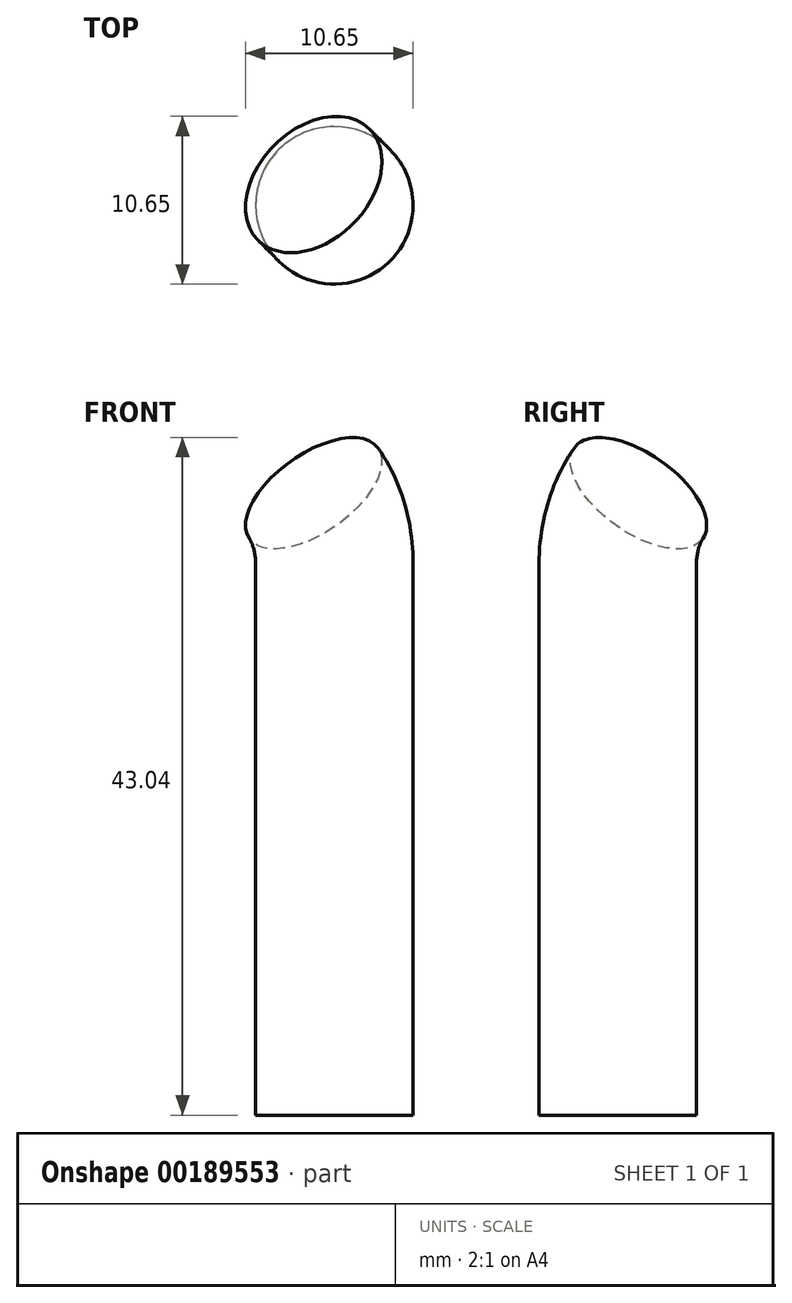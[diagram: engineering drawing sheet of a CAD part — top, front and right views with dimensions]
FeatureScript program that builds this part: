
annotation { "Feature Type Name" : "Feature", "Feature Type Description" : "" }
export const myFeature = defineFeature(function(context is Context, id is Id, definition is map)
    precondition{}
    {
        {
            var Q0;
            Q0=qCreatedBy(makeId("Top.planeOp"),FACE);
            var sketch = newSketch(context, id + "F0", { "sketchPlane" : qUnion([Q0])});
            skCircle(sketch, "E0", {"center": v(0, 0) * mm, "radius": 5 * mm});
            skSolve(sketch);
        }
        {
            var Q0;
            Q0=qCreatedBy(makeId("Top.planeOp"),FACE);
            var sketch = newSketch(context, id + "F1", { "sketchPlane" : qUnion([Q0])});
            skLineSegment(sketch, "E1", {"start": v(-3.65, 3.76) * mm, "end": v(-4.37, 4.46) * mm});
            skLineSegment(sketch, "E2", {"start": v(0, 9) * mm, "end": v(-9, 0) * mm});
            skSolve(sketch);
        }
        {
            var Q0;
            Q0=makeQuery(id+"F0.imprint","IMPRINT",FACE,{"disambiguationData":[TD([[makeQuery(id+"F0.imprint","IMPRINT",EDGE,{"derivedFrom":sQuery(id+"F0.wireOp",EDGE,"E0")}),1.0]])]});
            var Q1;
            Q1=sQuery(id+"F1.wireOp",EDGE,"E2");
            revolve(context, id + "F2", {"entities" : qUnion([Q0]), "axis" : qUnion([Q1]), "revolveType" : RevolveType.ONE_DIRECTION, "angle" : 45 * degree});
        }
        {
            var Q0;
            Q0=qCreatedBy(makeId("Right.planeOp"),FACE);
            var sketch = newSketch(context, id + "F3", { "sketchPlane" : qUnion([Q0])});
            skSolve(sketch);
        }
        {
            var Q0;
            Q0=makeQuery(id+"F2.opRevolve","CAP_FACE",FACE,{"disambiguationData":[OSD([sQuery(id+"F0.wireOp",EDGE,"E0")])],"isStart":true});
            var Q1;
            Q1=qSketchRegion(id+"F3",true);
            extrude(context, id + "F4", {"entities" : qUnion([Q0, Q1]), "operationType" : NewBodyOperationType.ADD, "depth" : 35 * mm});
        }
    });
